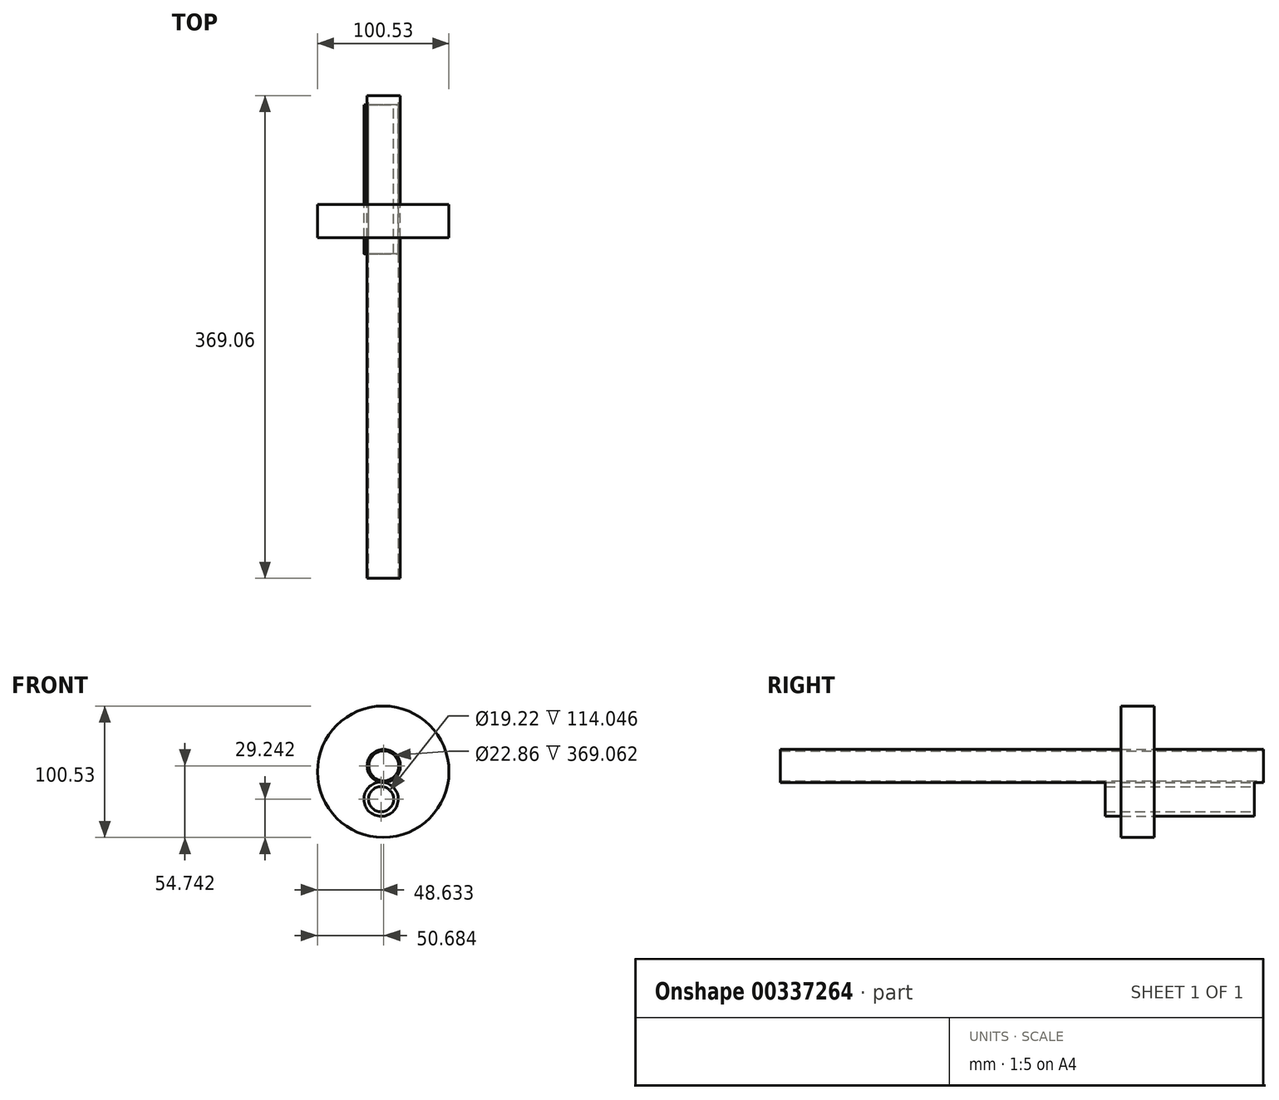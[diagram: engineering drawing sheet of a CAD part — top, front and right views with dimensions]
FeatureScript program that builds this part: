
annotation { "Feature Type Name" : "Feature", "Feature Type Description" : "" }
export const myFeature = defineFeature(function(context is Context, id is Id, definition is map)
    precondition{}
    {
        {
            var Q0;
            Q0=qCreatedBy(makeId("Front.planeOp"),FACE);
            var sketch = newSketch(context, id + "F0", { "sketchPlane" : qUnion([Q0])});
            skCircle(sketch, "E0", {"center": v(0, 0) * mm, "radius": 11.43 * mm});
            skCircle(sketch, "E1", {"center": v(0, 0) * mm, "radius": 12.7 * mm});
            skSolve(sketch);
        }
        {
            var Q0;
            Q0=makeQuery(id+"F0.imprint","IMPRINT",FACE,{"disambiguationData":[TD([[makeQuery(id+"F0.imprint","IMPRINT",EDGE,{"derivedFrom":sQuery(id+"F0.wireOp",EDGE,"E0")}),-1.0]])]});
            extrude(context, id + "F1", {"entities" : qUnion([Q0]), "depth" : 285.75 * mm, "hasSecondDirection" : true, "secondDirectionOppositeDirection" : true, "secondDirectionDepth" : 83.31 * mm});
        }
        {
            var Q0;
            Q0=qCreatedBy(makeId("Front.planeOp"),FACE);
            var sketch = newSketch(context, id + "F2", { "sketchPlane" : qUnion([Q0])});
            skCircle(sketch, "E2", {"center": v(-36.09, -27.28) * mm, "radius": 9.6 * mm});
            skCircle(sketch, "E3", {"center": v(-36.09, -27.28) * mm, "radius": 13.1 * mm});
            skSolve(sketch);
        }
        {
            var Q0;
            Q0 = qSketchRegion(id + "F2", true);
            extrude(context, id + "F3", {"entities" : qUnion([Q0]), "depth" : 37.6 * mm, "hasSecondDirection" : true, "secondDirectionOppositeDirection" : true, "secondDirectionDepth" : 76.45 * mm});
        }
        {
            var Q0;
            Q0=makeQuery(id+"F1.opExtrude","SWEPT_BODY",BODY,{"disambiguationData":[OSD([sQuery(id+"F0.wireOp",EDGE,"E0"),sQuery(id+"F0.wireOp",EDGE,"E1")])]});
            var Q1;
            Q1=makeQuery(id+"F3.opExtrude","CAP_EDGE",EDGE,{"disambiguationData":[OSD([sQuery(id+"F2.wireOp",EDGE,"E3")])],"isStart":false});
            var Q2;
            Q2=makeQuery(id+"F3.opExtrude","SWEPT_FACE",FACE,{"disambiguationData":[OSD([sQuery(id+"F2.wireOp",EDGE,"E3")])]});
            transform(context, id + "F4", {"entities" : qUnion([Q0]), "transformType" : TransformType.TRANSLATION_3D, "dx" : -34.04 * mm, "dy" : 0 * mm, "dz" : -1.78 * mm, "makeCopy" : false});
        }
        {
            var Q0;
            Q0=qCreatedBy(makeId("Front.planeOp"),FACE);
            var sketch = newSketch(context, id + "F5", { "sketchPlane" : qUnion([Q0])});
            skCircle(sketch, "E4", {"center": v(-34.46, -6.25) * mm, "radius": 50.27 * mm});
            skPoint(sketch, "E4.first.point", {"position": v(-79.9, 15.21) * mm});
            skPoint(sketch, "E4.second.point", {"position": v(-27.23, -56) * mm});
            skPoint(sketch, "E4.third.point", {"position": v(-9.73, -50.02) * mm});
            skSolve(sketch);
        }
        {
            var Q0;
            Q0 = qSketchRegion(id + "F5", true);
            extrude(context, id + "F6", {"entities" : qUnion([Q0]), "depth" : 25.4 * mm});
        }
    });
